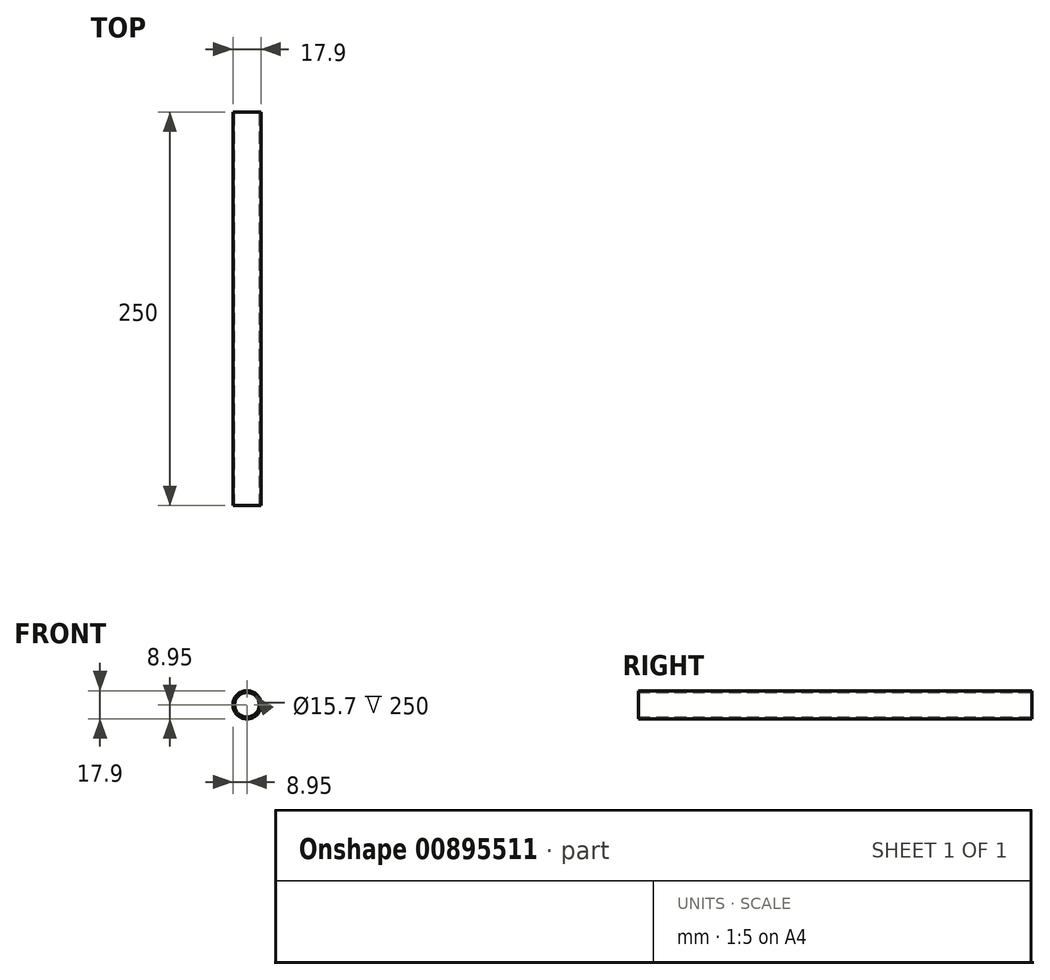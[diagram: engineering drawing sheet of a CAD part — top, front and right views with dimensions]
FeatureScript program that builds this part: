
annotation { "Feature Type Name" : "Feature", "Feature Type Description" : "" }
export const myFeature = defineFeature(function(context is Context, id is Id, definition is map)
    precondition{}
    {
        {
            var Q0;
            Q0=qCreatedBy(makeId("Front.planeOp"),FACE);
            var sketch = newSketch(context, id + "F0", { "sketchPlane" : qUnion([Q0])});
            skCircle(sketch, "E0", {"center": v(0, 0) * mm, "radius": 8.95 * mm});
            skCircle(sketch, "E1.0", {"center": v(0, 0) * mm, "radius": 7.85 * mm});
            skSolve(sketch);
        }
        {
            var Q0;
            Q0 = qSketchRegion(id + "F0", true);
            extrude(context, id + "F1", {"entities" : qUnion([Q0]), "depth" : 250 * mm, "offsetDistance" : 25 * mm});
        }
    });
